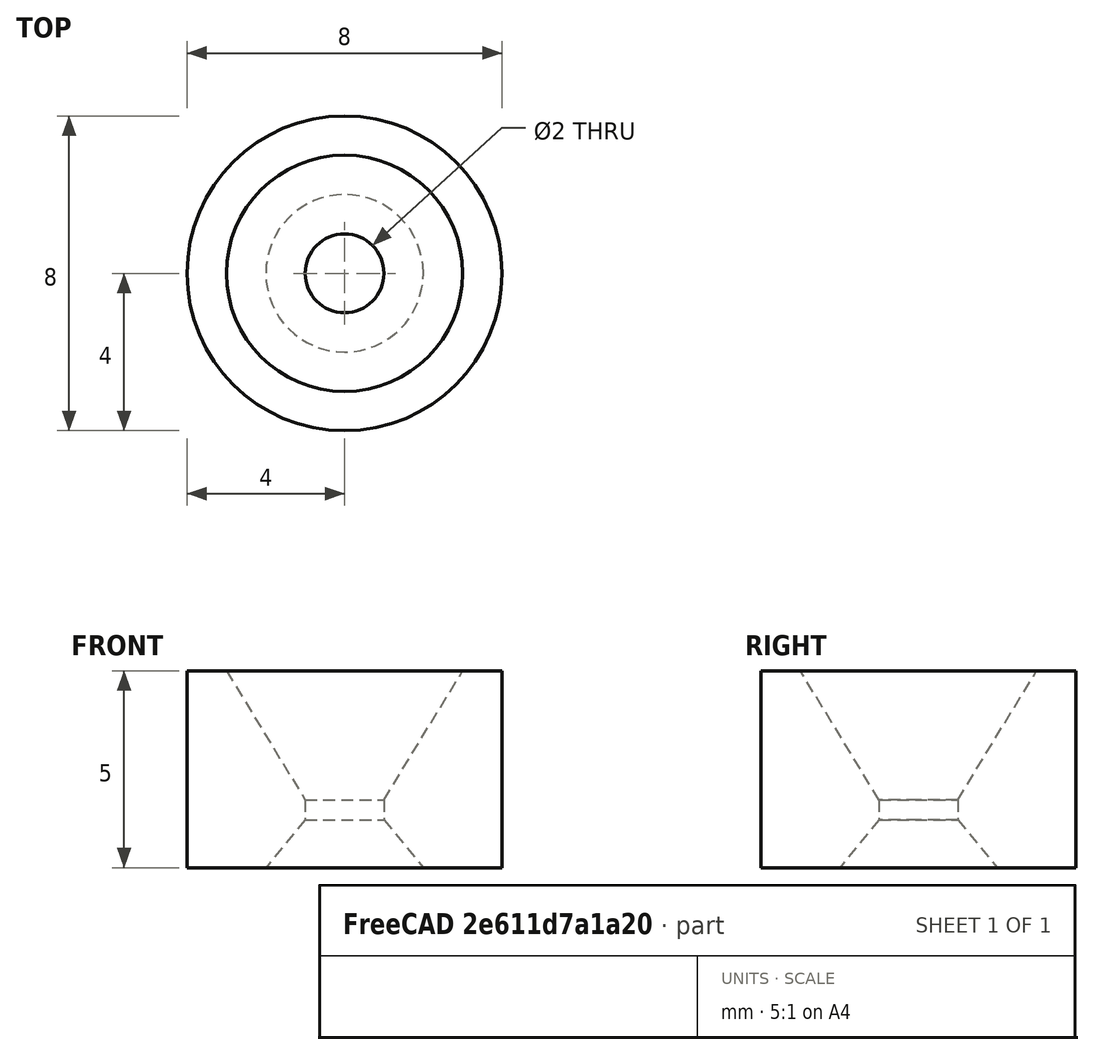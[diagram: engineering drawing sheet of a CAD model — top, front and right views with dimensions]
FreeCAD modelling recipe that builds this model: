
FCSTD DOCUMENT  (FreeCAD 0.18.4R)
Label: nozzle_small
Comment: # 2020-02-12 13:38:47: read from <userpath>/repositories/sussex_neuro/Olfactometer/hardware/mechanics/from_raiser_et_al/nozzle_small.ipt
License: All rights reserved
LicenseURL: http://en.wikipedia.org/wiki/All_rights_reserved
objects: Sketcher::SketchObject×2, Spreadsheet::Sheet×1, Part::Revolution×1
note: 3 computed .brp shape members not serialized (recipe doc carries the construction recipe); baked Part::Feature solids carry a one-line shape summary decoded from their .brp

FEATURE [Spreadsheet::Sheet] Parameters
  cells = A1=Parameter; B1=Value; C1=Fromula; D1=Tolerance; E1=Comment; A2=d13; B2(d13_)=90; C2=90°; D2=NOMINAL; A3=d16; B3(d16_)=1; C3=1mm; D3=NOMINAL; A4=d17; B4(d17_)=0.2; C4=0.2mm; D4=NOMINAL; A5=d18; B5(d18_)=2; C5=2mm; D5=NOMINAL; A6=d20; B6(d20_)=0.5; C6=0.5mm; D6=NOMINAL; A7=d21; B7(d21_)=2; C7=2mm; D7=NOMINAL; A8=d22; B8(d22_)=0; C8=0mm; D8=NOMINAL; A9=d23; B9(d23_)=20; C9=20mm; D9=NOMINAL; A10=d24; B10(d24_)=1; C10=1mm; D10=NOMINAL; A11=d25; B11(d25_)=4; C11=4mm; D11=NOMINAL; A12=d26; B12(d26_)=0.5; C12=0.5mm; D12=NOMINAL; A13=d27; B13(d27_)=2; C13=2mm; D13=NOMINAL; A14=d28; B14(d28_)=0; C14=0mm; D14=NOMINAL; A15=d29; B15(d29_)=20; C15=20mm; D15=NOMINAL; A16=d30; B16(d30_)=0.5; C16=0.5mm; D16=NOMINAL; A17=d31; B17(d31_)=2; C17=2mm; D17=NOMINAL; A18=d32; B18(d32_)=0; C18=0mm; D18=NOMINAL; A19=d33; B19(d33_)=20; C19=20mm; D19=NOMINAL; A20=d4; B20(d4_)=5; C20=5mm; D20=NOMINAL
FEATURE [Sketcher::SketchObject] Sketch2
  Placement = pos=(0,0,0) rot=(0,0.707107,0.707107;3.14159rad)
  sketch-geometry (8):
    g0: LineSegment StartX=4 StartY=0 StartZ=0 EndX=4 EndY=5 EndZ=0
    g1: LineSegment StartX=7e-16 StartY=-0.993601 StartZ=0 EndX=-1.5e-15 EndY=4.43052 EndZ=0
    g2: LineSegment StartX=4 StartY=5 StartZ=0 EndX=4 EndY=0 EndZ=0
    g3: LineSegment StartX=1 StartY=1.21846 StartZ=0 EndX=1 EndY=1.71846 EndZ=0
    g4: LineSegment StartX=1 StartY=1.21846 StartZ=0 EndX=2 EndY=-2.2e-15 EndZ=0
    g5: LineSegment StartX=2 StartY=-2.3e-15 StartZ=0 EndX=4 EndY=0 EndZ=0
    g6: LineSegment StartX=4 StartY=5 StartZ=0 EndX=3 EndY=5 EndZ=0
    g7: LineSegment StartX=3 StartY=5 StartZ=0 EndX=1 EndY=1.71846 EndZ=0
  constraints (7):
    c: Parallel(g2,g3)
    c: Perpendicular(g3,g5)
    c: Parallel(g5,g6)
    c: Coincident(g0,g2)
    c: Coincident(g0,g5)
    c: Coincident(g0,g2)
    c: Coincident(g0,g6)
FEATURE [Sketcher::SketchObject] Sketch2_bp
  Placement = pos=(0,0,0) rot=(0,0.707107,0.707107;3.14159rad)
  sketch-geometry (6):
    g0: LineSegment StartX=4 StartY=0 StartZ=0 EndX=4 EndY=5 EndZ=0
    g1: LineSegment StartX=4 StartY=5 StartZ=0 EndX=3 EndY=5 EndZ=0
    g2: LineSegment StartX=3 StartY=5 StartZ=0 EndX=1 EndY=1.71846 EndZ=0
    g3: LineSegment StartX=1 StartY=1.71846 StartZ=0 EndX=1 EndY=1.21846 EndZ=0
    g4: LineSegment StartX=1 StartY=1.21846 StartZ=0 EndX=2 EndY=-2.2e-15 EndZ=0
    g5: LineSegment StartX=2 StartY=-2.3e-15 StartZ=0 EndX=4 EndY=0 EndZ=0
FEATURE [Part::Revolution] Revolution2
  Angle = 360
  Axis = (2e-16,0,0.542412)
  Base = (-7e-16,0,-0.993601)
  FaceMakerClass = Part::FaceMakerBullseye
  Solid = true
  Source = -> Sketch2_bp
  Symmetric = false
